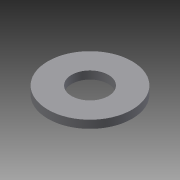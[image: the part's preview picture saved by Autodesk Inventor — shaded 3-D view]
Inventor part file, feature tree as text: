
AUTODESK INVENTOR PART (.ipt)
format: ipt  version: 2015 SP1 (Build 190203100, 203)  size: 74,240 bytes
history: native  units: in
note: dims shown in document units (in); Inventor stores cm internally (conversion verified against a paired STEP export)
features: extrude x1, sketch x1
ambient origin geometry x8: Origin, YZ Plane, XZ Plane, XY Plane, X Axis, Y Axis, Z Axis, Center Point
bodies: Solid1 (feature_tree)
feature tree (2):
  extrude  "Extrusion1"  Depth=0.0938in
  sketch  "Sketch1"  dims[d0=0.4375in d1=1.0in d2=0.0938in d3=0.0in]
